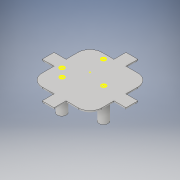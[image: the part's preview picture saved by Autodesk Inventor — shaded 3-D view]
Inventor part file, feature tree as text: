
AUTODESK INVENTOR PART (.ipt)
format: ipt  version: 2018 (Build 220112000, 112)  size: 1,730,560 bytes
history: native  units: in
note: dims shown in document units (in); Inventor stores cm internally (conversion verified against a paired STEP export)
features: other x4, fillet x3, sketch x3, extrude x2, move_body x1, emboss x1
ambient origin geometry x8: Origin, YZ Plane, XZ Plane, XY Plane, X Axis, Y Axis, Z Axis, Center Point
bodies: Solid5 (feature_tree)
feature tree (14):
  other  "Remote Bottom.ipt"
  move_body  "Move Body2"
  extrude  "Extrusion1"  Depth=1.25in
  extrude  "Extrusion2"  Depth=1.25in
  fillet  "Fillet3"  Radius=1.25in
  fillet  "Fillet6"  Radius=0.5in
  fillet  "Fillet7"  Radius=0.5in
  emboss  "Emboss1"
  sketch  "Sketch2"  dims[d12=1.0in d13=0.0in d14=1.25in]
  sketch  "Sketch3"  dims[d15=1.25in d16=1.25in d17=1.25in d18=0.5in d19=0.5in]
  other  "Magnet Sketch_1"
  other  "Solid1::Remote Bottom.ipt"
  other  "TaggingFeature3"
  sketch  "Sketch5"  dims[d20=0.5in d21=0.25in d22=1.5748in d24=360.0deg d26=0.125in d27=0.0in d30=0.125in d33=0.3937in d34=0.125in d35=0.125in d36=0.125in d37=0.125in d38=0.01in d39=0.01in d40=0.01in d41=0.01in d42=0.0in d43=-1.0in d44=0.0in d45=0.175in d46=0.1in d47=0.05in d48=0.0in]
